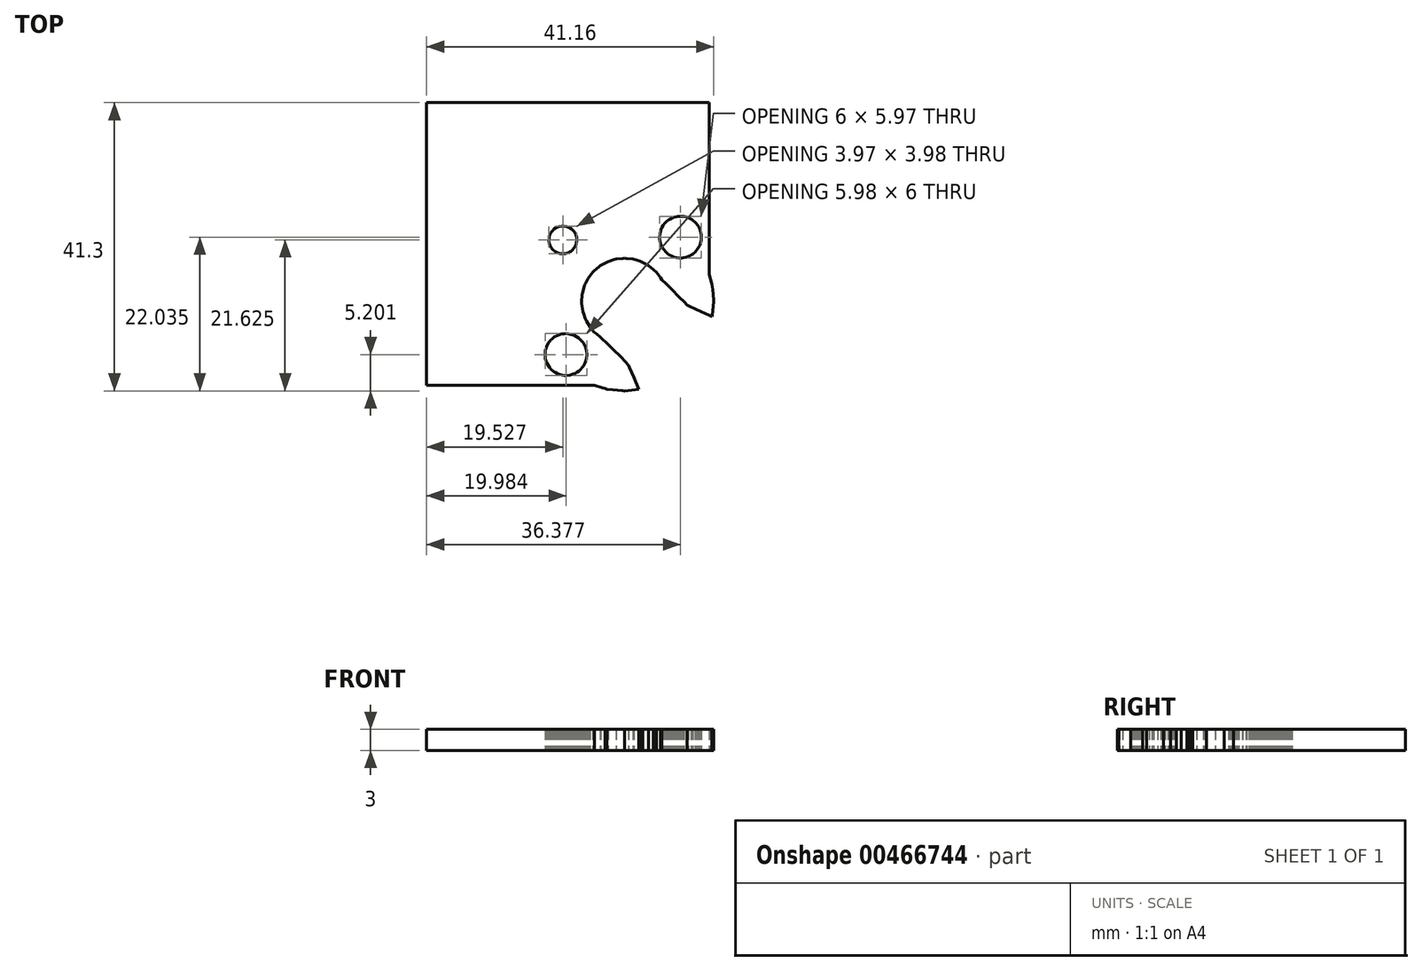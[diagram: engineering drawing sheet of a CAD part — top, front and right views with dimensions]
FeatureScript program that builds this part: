
annotation { "Feature Type Name" : "Feature", "Feature Type Description" : "" }
export const myFeature = defineFeature(function(context is Context, id is Id, definition is map)
    precondition{}
    {
        {
            var Q0;
            Q0=qCreatedBy(makeId("Top.planeOp"),FACE);
            var sketch = newSketch(context, id + "F0", { "sketchPlane" : qUnion([Q0])});
            skLineSegment(sketch, "E0", {"start": v(-20.58, -19.85) * mm, "end": v(-20.58, 20.65) * mm});
            skLineSegment(sketch, "E1", {"start": v(-20.58, 20.65) * mm, "end": v(19.92, 20.65) * mm});
            skLineSegment(sketch, "E2", {"start": v(19.92, 20.65) * mm, "end": v(19.92, -4) * mm});
            skLineSegment(sketch, "E3", {"start": v(19.92, -4) * mm, "end": v(20.25, -5.09) * mm});
            skLineSegment(sketch, "E4", {"start": v(20.25, -5.09) * mm, "end": v(20.33, -5.35) * mm});
            skLineSegment(sketch, "E5", {"start": v(20.33, -5.35) * mm, "end": v(20.4, -6.13) * mm});
            skLineSegment(sketch, "E6", {"start": v(20.4, -6.13) * mm, "end": v(20.55, -7.57) * mm});
            skLineSegment(sketch, "E7", {"start": v(20.55, -7.57) * mm, "end": v(20.58, -7.85) * mm});
            skLineSegment(sketch, "E8", {"start": v(20.58, -7.85) * mm, "end": v(20.38, -9.83) * mm});
            skLineSegment(sketch, "E9", {"start": v(20.38, -9.83) * mm, "end": v(20.3, -10.01) * mm});
            skLineSegment(sketch, "E10", {"start": v(20.3, -10.01) * mm, "end": v(19.9, -9.82) * mm});
            skLineSegment(sketch, "E11", {"start": v(19.9, -9.82) * mm, "end": v(18.76, -9.29) * mm});
            skLineSegment(sketch, "E12", {"start": v(18.76, -9.29) * mm, "end": v(17.15, -8.53) * mm});
            skLineSegment(sketch, "E13", {"start": v(17.15, -8.53) * mm, "end": v(16.75, -8.34) * mm});
            skLineSegment(sketch, "E14", {"start": v(16.75, -8.34) * mm, "end": v(16.35, -7.93) * mm});
            skLineSegment(sketch, "E15", {"start": v(16.35, -7.93) * mm, "end": v(15.6, -7.2) * mm});
            skLineSegment(sketch, "E16", {"start": v(15.6, -7.2) * mm, "end": v(14.5, -6.08) * mm});
            skLineSegment(sketch, "E17", {"start": v(14.5, -6.08) * mm, "end": v(14.13, -5.71) * mm});
            skLineSegment(sketch, "E18", {"start": v(14.13, -5.71) * mm, "end": v(13.74, -5.33) * mm});
            skLineSegment(sketch, "E19", {"start": v(13.74, -5.33) * mm, "end": v(13.12, -4.7) * mm});
            skLineSegment(sketch, "E20", {"start": v(13.12, -4.7) * mm, "end": v(12.95, -4.4) * mm});
            skLineSegment(sketch, "E21", {"start": v(12.95, -4.4) * mm, "end": v(12.37, -3.69) * mm});
            skLineSegment(sketch, "E22", {"start": v(12.37, -3.69) * mm, "end": v(11.95, -3.26) * mm});
            skLineSegment(sketch, "E23", {"start": v(11.95, -3.26) * mm, "end": v(11.25, -2.68) * mm});
            skLineSegment(sketch, "E24", {"start": v(11.25, -2.68) * mm, "end": v(10.4, -2.23) * mm});
            skLineSegment(sketch, "E25", {"start": v(10.4, -2.23) * mm, "end": v(10.03, -2.07) * mm});
            skLineSegment(sketch, "E26", {"start": v(10.03, -2.07) * mm, "end": v(9.6, -1.94) * mm});
            skLineSegment(sketch, "E27", {"start": v(9.6, -1.94) * mm, "end": v(9.01, -1.76) * mm});
            skLineSegment(sketch, "E28", {"start": v(9.01, -1.76) * mm, "end": v(8.06, -1.67) * mm});
            skLineSegment(sketch, "E29", {"start": v(8.06, -1.67) * mm, "end": v(7.8, -1.64) * mm});
            skLineSegment(sketch, "E30", {"start": v(7.8, -1.64) * mm, "end": v(7.55, -1.67) * mm});
            skLineSegment(sketch, "E31", {"start": v(7.55, -1.67) * mm, "end": v(6.6, -1.76) * mm});
            skLineSegment(sketch, "E32", {"start": v(6.6, -1.76) * mm, "end": v(6.35, -1.84) * mm});
            skLineSegment(sketch, "E33", {"start": v(6.35, -1.84) * mm, "end": v(5.44, -2.11) * mm});
            skLineSegment(sketch, "E34", {"start": v(5.44, -2.11) * mm, "end": v(5.2, -2.23) * mm});
            skLineSegment(sketch, "E35", {"start": v(5.2, -2.23) * mm, "end": v(4.32, -2.72) * mm});
            skLineSegment(sketch, "E36", {"start": v(4.32, -2.72) * mm, "end": v(4.17, -2.85) * mm});
            skLineSegment(sketch, "E37", {"start": v(4.17, -2.85) * mm, "end": v(3.77, -3.18) * mm});
            skLineSegment(sketch, "E38", {"start": v(3.77, -3.18) * mm, "end": v(3.43, -3.45) * mm});
            skLineSegment(sketch, "E39", {"start": v(3.43, -3.45) * mm, "end": v(3.24, -3.69) * mm});
            skLineSegment(sketch, "E40", {"start": v(3.24, -3.69) * mm, "end": v(2.63, -4.44) * mm});
            skLineSegment(sketch, "E41", {"start": v(2.63, -4.44) * mm, "end": v(2.54, -4.62) * mm});
            skLineSegment(sketch, "E42", {"start": v(2.54, -4.62) * mm, "end": v(2.2, -5.26) * mm});
            skLineSegment(sketch, "E43", {"start": v(2.2, -5.26) * mm, "end": v(2.09, -5.46) * mm});
            skLineSegment(sketch, "E44", {"start": v(2.09, -5.46) * mm, "end": v(2.01, -5.7) * mm});
            skLineSegment(sketch, "E45", {"start": v(2.01, -5.7) * mm, "end": v(1.74, -6.62) * mm});
            skLineSegment(sketch, "E46", {"start": v(1.74, -6.62) * mm, "end": v(1.71, -6.88) * mm});
            skLineSegment(sketch, "E47", {"start": v(1.71, -6.88) * mm, "end": v(1.62, -7.83) * mm});
            skLineSegment(sketch, "E48", {"start": v(1.62, -7.83) * mm, "end": v(1.64, -8.09) * mm});
            skLineSegment(sketch, "E49", {"start": v(1.64, -8.09) * mm, "end": v(1.81, -9.28) * mm});
            skLineSegment(sketch, "E50", {"start": v(1.81, -9.28) * mm, "end": v(1.92, -9.63) * mm});
            skLineSegment(sketch, "E51", {"start": v(1.92, -9.63) * mm, "end": v(2.11, -10.24) * mm});
            skLineSegment(sketch, "E52", {"start": v(2.11, -10.24) * mm, "end": v(2.34, -10.67) * mm});
            skLineSegment(sketch, "E53", {"start": v(2.34, -10.67) * mm, "end": v(2.83, -11.46) * mm});
            skLineSegment(sketch, "E54", {"start": v(2.83, -11.46) * mm, "end": v(3.17, -11.9) * mm});
            skLineSegment(sketch, "E55", {"start": v(3.17, -11.9) * mm, "end": v(3.43, -12.2) * mm});
            skLineSegment(sketch, "E56", {"start": v(3.43, -12.2) * mm, "end": v(3.77, -12.48) * mm});
            skLineSegment(sketch, "E57", {"start": v(3.77, -12.48) * mm, "end": v(4.37, -12.97) * mm});
            skLineSegment(sketch, "E58", {"start": v(4.37, -12.97) * mm, "end": v(5.44, -14) * mm});
            skLineSegment(sketch, "E59", {"start": v(5.44, -14) * mm, "end": v(6.14, -14.7) * mm});
            skLineSegment(sketch, "E60", {"start": v(6.14, -14.7) * mm, "end": v(7.25, -15.8) * mm});
            skLineSegment(sketch, "E61", {"start": v(7.25, -15.8) * mm, "end": v(7.85, -16.41) * mm});
            skLineSegment(sketch, "E62", {"start": v(7.85, -16.41) * mm, "end": v(8.34, -17) * mm});
            skLineSegment(sketch, "E63", {"start": v(8.34, -17) * mm, "end": v(8.5, -17.33) * mm});
            skLineSegment(sketch, "E64", {"start": v(8.5, -17.33) * mm, "end": v(9.15, -18.7) * mm});
            skLineSegment(sketch, "E65", {"start": v(9.15, -18.7) * mm, "end": v(9.83, -20.45) * mm});
            skLineSegment(sketch, "E66", {"start": v(9.83, -20.45) * mm, "end": v(7.78, -20.65) * mm});
            skLineSegment(sketch, "E67", {"start": v(7.78, -20.65) * mm, "end": v(7.5, -20.62) * mm});
            skLineSegment(sketch, "E68", {"start": v(7.5, -20.62) * mm, "end": v(6.06, -20.48) * mm});
            skLineSegment(sketch, "E69", {"start": v(6.06, -20.48) * mm, "end": v(5.28, -20.4) * mm});
            skLineSegment(sketch, "E70", {"start": v(5.28, -20.4) * mm, "end": v(5.02, -20.32) * mm});
            skLineSegment(sketch, "E71", {"start": v(5.02, -20.32) * mm, "end": v(4.68, -20.22) * mm});
            skLineSegment(sketch, "E72", {"start": v(4.68, -20.22) * mm, "end": v(3.45, -19.85) * mm});
            skLineSegment(sketch, "E73", {"start": v(3.45, -19.85) * mm, "end": v(-20.58, -19.85) * mm});
            skLineSegment(sketch, "E74", {"start": v(-3.59, -15.66) * mm, "end": v(-3.55, -14.86) * mm});
            skLineSegment(sketch, "E75", {"start": v(-3.55, -14.86) * mm, "end": v(-3.46, -14.58) * mm});
            skLineSegment(sketch, "E76", {"start": v(-3.46, -14.58) * mm, "end": v(-3.38, -14.3) * mm});
            skLineSegment(sketch, "E77", {"start": v(-3.38, -14.3) * mm, "end": v(-3.1, -13.78) * mm});
            skLineSegment(sketch, "E78", {"start": v(-3.1, -13.78) * mm, "end": v(-2.91, -13.55) * mm});
            skLineSegment(sketch, "E79", {"start": v(-2.91, -13.55) * mm, "end": v(-2.78, -13.4) * mm});
            skLineSegment(sketch, "E80", {"start": v(-2.78, -13.4) * mm, "end": v(-2.65, -13.26) * mm});
            skLineSegment(sketch, "E81", {"start": v(-2.65, -13.26) * mm, "end": v(-2.27, -12.95) * mm});
            skLineSegment(sketch, "E82", {"start": v(-2.27, -12.95) * mm, "end": v(-1.75, -12.68) * mm});
            skLineSegment(sketch, "E83", {"start": v(-1.75, -12.68) * mm, "end": v(-1.2, -12.5) * mm});
            skLineSegment(sketch, "E84", {"start": v(-1.2, -12.5) * mm, "end": v(-0.86, -12.47) * mm});
            skLineSegment(sketch, "E85", {"start": v(-0.86, -12.47) * mm, "end": v(-0.6, -12.45) * mm});
            skLineSegment(sketch, "E86", {"start": v(-0.6, -12.45) * mm, "end": v(-0.27, -12.48) * mm});
            skLineSegment(sketch, "E87", {"start": v(-0.27, -12.48) * mm, "end": v(-0.02, -12.52) * mm});
            skLineSegment(sketch, "E88", {"start": v(-0.02, -12.52) * mm, "end": v(0.24, -12.59) * mm});
            skLineSegment(sketch, "E89", {"start": v(0.24, -12.59) * mm, "end": v(0.54, -12.68) * mm});
            skLineSegment(sketch, "E90", {"start": v(0.54, -12.68) * mm, "end": v(0.84, -12.84) * mm});
            skLineSegment(sketch, "E91", {"start": v(0.84, -12.84) * mm, "end": v(1.18, -13.05) * mm});
            skLineSegment(sketch, "E92", {"start": v(1.18, -13.05) * mm, "end": v(1.59, -13.42) * mm});
            skLineSegment(sketch, "E93", {"start": v(1.59, -13.42) * mm, "end": v(1.89, -13.78) * mm});
            skLineSegment(sketch, "E94", {"start": v(1.89, -13.78) * mm, "end": v(2.08, -14.15) * mm});
            skLineSegment(sketch, "E95", {"start": v(2.08, -14.15) * mm, "end": v(2.2, -14.4) * mm});
            skLineSegment(sketch, "E96", {"start": v(2.2, -14.4) * mm, "end": v(2.34, -14.86) * mm});
            skLineSegment(sketch, "E97", {"start": v(2.34, -14.86) * mm, "end": v(2.4, -15.45) * mm});
            skLineSegment(sketch, "E98", {"start": v(2.4, -15.45) * mm, "end": v(2.34, -16.03) * mm});
            skLineSegment(sketch, "E99", {"start": v(2.34, -16.03) * mm, "end": v(2.16, -16.6) * mm});
            skLineSegment(sketch, "E100", {"start": v(2.16, -16.6) * mm, "end": v(2.03, -16.86) * mm});
            skLineSegment(sketch, "E101", {"start": v(2.03, -16.86) * mm, "end": v(1.89, -17.11) * mm});
            skLineSegment(sketch, "E102", {"start": v(1.89, -17.11) * mm, "end": v(1.72, -17.32) * mm});
            skLineSegment(sketch, "E103", {"start": v(1.72, -17.32) * mm, "end": v(1.5, -17.58) * mm});
            skLineSegment(sketch, "E104", {"start": v(1.5, -17.58) * mm, "end": v(1.22, -17.8) * mm});
            skLineSegment(sketch, "E105", {"start": v(1.22, -17.8) * mm, "end": v(0.96, -18) * mm});
            skLineSegment(sketch, "E106", {"start": v(0.96, -18) * mm, "end": v(0.72, -18.12) * mm});
            skLineSegment(sketch, "E107", {"start": v(0.72, -18.12) * mm, "end": v(0.51, -18.23) * mm});
            skLineSegment(sketch, "E108", {"start": v(0.51, -18.23) * mm, "end": v(-0.04, -18.4) * mm});
            skLineSegment(sketch, "E109", {"start": v(-0.04, -18.4) * mm, "end": v(-0.6, -18.45) * mm});
            skLineSegment(sketch, "E110", {"start": v(-0.6, -18.45) * mm, "end": v(-0.86, -18.42) * mm});
            skLineSegment(sketch, "E111", {"start": v(-0.86, -18.42) * mm, "end": v(-1.17, -18.4) * mm});
            skLineSegment(sketch, "E112", {"start": v(-1.17, -18.4) * mm, "end": v(-1.44, -18.32) * mm});
            skLineSegment(sketch, "E113", {"start": v(-1.44, -18.32) * mm, "end": v(-1.8, -18.2) * mm});
            skLineSegment(sketch, "E114", {"start": v(-1.8, -18.2) * mm, "end": v(-2.1, -18.04) * mm});
            skLineSegment(sketch, "E115", {"start": v(-2.1, -18.04) * mm, "end": v(-2.38, -17.85) * mm});
            skLineSegment(sketch, "E116", {"start": v(-2.38, -17.85) * mm, "end": v(-2.73, -17.57) * mm});
            skLineSegment(sketch, "E117", {"start": v(-2.73, -17.57) * mm, "end": v(-2.95, -17.3) * mm});
            skLineSegment(sketch, "E118", {"start": v(-2.95, -17.3) * mm, "end": v(-3.38, -16.6) * mm});
            skLineSegment(sketch, "E119", {"start": v(-3.38, -16.6) * mm, "end": v(-3.55, -16.03) * mm});
            skLineSegment(sketch, "E120", {"start": v(-3.55, -16.03) * mm, "end": v(-3.59, -15.66) * mm});
            skLineSegment(sketch, "E121", {"start": v(-3.04, 0.82) * mm, "end": v(-3.03, 1.21) * mm});
            skLineSegment(sketch, "E122", {"start": v(-3.03, 1.21) * mm, "end": v(-2.98, 1.48) * mm});
            skLineSegment(sketch, "E123", {"start": v(-2.98, 1.48) * mm, "end": v(-2.93, 1.68) * mm});
            skLineSegment(sketch, "E124", {"start": v(-2.93, 1.68) * mm, "end": v(-2.8, 1.95) * mm});
            skLineSegment(sketch, "E125", {"start": v(-2.8, 1.95) * mm, "end": v(-2.7, 2.12) * mm});
            skLineSegment(sketch, "E126", {"start": v(-2.7, 2.12) * mm, "end": v(-2.57, 2.27) * mm});
            skLineSegment(sketch, "E127", {"start": v(-2.57, 2.27) * mm, "end": v(-2.29, 2.54) * mm});
            skLineSegment(sketch, "E128", {"start": v(-2.29, 2.54) * mm, "end": v(-1.96, 2.76) * mm});
            skLineSegment(sketch, "E129", {"start": v(-1.96, 2.76) * mm, "end": v(-1.6, 2.9) * mm});
            skLineSegment(sketch, "E130", {"start": v(-1.6, 2.9) * mm, "end": v(-1.21, 2.97) * mm});
            skLineSegment(sketch, "E131", {"start": v(-1.21, 2.97) * mm, "end": v(-0.9, 2.97) * mm});
            skLineSegment(sketch, "E132", {"start": v(-0.9, 2.97) * mm, "end": v(-0.51, 2.9) * mm});
            skLineSegment(sketch, "E133", {"start": v(-0.51, 2.9) * mm, "end": v(-0.15, 2.76) * mm});
            skLineSegment(sketch, "E134", {"start": v(-0.15, 2.76) * mm, "end": v(0.18, 2.54) * mm});
            skLineSegment(sketch, "E135", {"start": v(0.18, 2.54) * mm, "end": v(0.6, 2.1) * mm});
            skLineSegment(sketch, "E136", {"start": v(0.6, 2.1) * mm, "end": v(0.8, 1.75) * mm});
            skLineSegment(sketch, "E137", {"start": v(0.8, 1.75) * mm, "end": v(0.9, 1.37) * mm});
            skLineSegment(sketch, "E138", {"start": v(0.9, 1.37) * mm, "end": v(0.93, 1.1) * mm});
            skLineSegment(sketch, "E139", {"start": v(0.93, 1.1) * mm, "end": v(0.93, 0.8) * mm});
            skLineSegment(sketch, "E140", {"start": v(0.93, 0.8) * mm, "end": v(0.9, 0.57) * mm});
            skLineSegment(sketch, "E141", {"start": v(0.9, 0.57) * mm, "end": v(0.84, 0.38) * mm});
            skLineSegment(sketch, "E142", {"start": v(0.84, 0.38) * mm, "end": v(0.72, 0.08) * mm});
            skLineSegment(sketch, "E143", {"start": v(0.72, 0.08) * mm, "end": v(0.5, -0.25) * mm});
            skLineSegment(sketch, "E144", {"start": v(0.5, -0.25) * mm, "end": v(0.39, -0.4) * mm});
            skLineSegment(sketch, "E145", {"start": v(0.39, -0.4) * mm, "end": v(0.23, -0.53) * mm});
            skLineSegment(sketch, "E146", {"start": v(0.23, -0.53) * mm, "end": v(0.08, -0.66) * mm});
            skLineSegment(sketch, "E147", {"start": v(0.08, -0.66) * mm, "end": v(-0.1, -0.77) * mm});
            skLineSegment(sketch, "E148", {"start": v(-0.1, -0.77) * mm, "end": v(-0.29, -0.86) * mm});
            skLineSegment(sketch, "E149", {"start": v(-0.29, -0.86) * mm, "end": v(-0.51, -0.93) * mm});
            skLineSegment(sketch, "E150", {"start": v(-0.51, -0.93) * mm, "end": v(-0.74, -0.99) * mm});
            skLineSegment(sketch, "E151", {"start": v(-0.74, -0.99) * mm, "end": v(-1.06, -1.02) * mm});
            skLineSegment(sketch, "E152", {"start": v(-1.06, -1.02) * mm, "end": v(-1.45, -0.98) * mm});
            skLineSegment(sketch, "E153", {"start": v(-1.45, -0.98) * mm, "end": v(-1.82, -0.87) * mm});
            skLineSegment(sketch, "E154", {"start": v(-1.82, -0.86) * mm, "end": v(-2.17, -0.68) * mm});
            skLineSegment(sketch, "E155", {"start": v(-2.17, -0.68) * mm, "end": v(-2.47, -0.43) * mm});
            skLineSegment(sketch, "E156", {"start": v(-2.47, -0.43) * mm, "end": v(-2.72, -0.13) * mm});
            skLineSegment(sketch, "E157", {"start": v(-2.72, -0.13) * mm, "end": v(-2.87, 0.15) * mm});
            skLineSegment(sketch, "E158", {"start": v(-2.87, 0.15) * mm, "end": v(-2.97, 0.44) * mm});
            skLineSegment(sketch, "E159", {"start": v(-2.97, 0.44) * mm, "end": v(-3.04, 0.82) * mm});
            skLineSegment(sketch, "E160", {"start": v(12.8, 1.38) * mm, "end": v(12.85, 1.87) * mm});
            skLineSegment(sketch, "E161", {"start": v(12.85, 1.87) * mm, "end": v(13, 2.47) * mm});
            skLineSegment(sketch, "E162", {"start": v(13, 2.47) * mm, "end": v(13.16, 2.78) * mm});
            skLineSegment(sketch, "E163", {"start": v(13.16, 2.78) * mm, "end": v(13.3, 3.05) * mm});
            skLineSegment(sketch, "E164", {"start": v(13.3, 3.05) * mm, "end": v(13.54, 3.33) * mm});
            skLineSegment(sketch, "E165", {"start": v(13.54, 3.33) * mm, "end": v(13.65, 3.47) * mm});
            skLineSegment(sketch, "E166", {"start": v(13.65, 3.47) * mm, "end": v(13.84, 3.63) * mm});
            skLineSegment(sketch, "E167", {"start": v(13.84, 3.63) * mm, "end": v(14.05, 3.81) * mm});
            skLineSegment(sketch, "E168", {"start": v(14.05, 3.81) * mm, "end": v(14.34, 3.99) * mm});
            skLineSegment(sketch, "E169", {"start": v(14.34, 3.99) * mm, "end": v(14.62, 4.14) * mm});
            skLineSegment(sketch, "E170", {"start": v(14.62, 4.14) * mm, "end": v(14.86, 4.22) * mm});
            skLineSegment(sketch, "E171", {"start": v(14.86, 4.22) * mm, "end": v(15.14, 4.3) * mm});
            skLineSegment(sketch, "E172", {"start": v(15.14, 4.3) * mm, "end": v(15.4, 4.34) * mm});
            skLineSegment(sketch, "E173", {"start": v(15.4, 4.34) * mm, "end": v(15.7, 4.37) * mm});
            skLineSegment(sketch, "E174", {"start": v(15.7, 4.37) * mm, "end": v(16.01, 4.36) * mm});
            skLineSegment(sketch, "E175", {"start": v(16.01, 4.36) * mm, "end": v(16.27, 4.33) * mm});
            skLineSegment(sketch, "E176", {"start": v(16.27, 4.33) * mm, "end": v(16.6, 4.25) * mm});
            skLineSegment(sketch, "E177", {"start": v(16.6, 4.25) * mm, "end": v(16.93, 4.16) * mm});
            skLineSegment(sketch, "E178", {"start": v(16.93, 4.16) * mm, "end": v(17.2, 4.01) * mm});
            skLineSegment(sketch, "E179", {"start": v(17.2, 4.01) * mm, "end": v(17.46, 3.88) * mm});
            skLineSegment(sketch, "E180", {"start": v(17.46, 3.88) * mm, "end": v(18.01, 3.39) * mm});
            skLineSegment(sketch, "E181", {"start": v(18.01, 3.39) * mm, "end": v(18.26, 3.08) * mm});
            skLineSegment(sketch, "E182", {"start": v(18.26, 3.08) * mm, "end": v(18.43, 2.8) * mm});
            skLineSegment(sketch, "E183", {"start": v(18.43, 2.8) * mm, "end": v(18.58, 2.5) * mm});
            skLineSegment(sketch, "E184", {"start": v(18.58, 2.5) * mm, "end": v(18.74, 1.96) * mm});
            skLineSegment(sketch, "E185", {"start": v(18.74, 1.96) * mm, "end": v(18.76, 1.71) * mm});
            skLineSegment(sketch, "E186", {"start": v(18.76, 1.71) * mm, "end": v(18.8, 1.37) * mm});
            skLineSegment(sketch, "E187", {"start": v(18.8, 1.37) * mm, "end": v(18.76, 1) * mm});
            skLineSegment(sketch, "E188", {"start": v(18.76, 1) * mm, "end": v(18.7, 0.67) * mm});
            skLineSegment(sketch, "E189", {"start": v(18.7, 0.67) * mm, "end": v(18.57, 0.23) * mm});
            skLineSegment(sketch, "E190", {"start": v(18.57, 0.23) * mm, "end": v(18.37, -0.15) * mm});
            skLineSegment(sketch, "E191", {"start": v(18.37, -0.15) * mm, "end": v(18.24, -0.35) * mm});
            skLineSegment(sketch, "E192", {"start": v(18.24, -0.35) * mm, "end": v(18.05, -0.58) * mm});
            skLineSegment(sketch, "E193", {"start": v(18.05, -0.58) * mm, "end": v(17.87, -0.78) * mm});
            skLineSegment(sketch, "E194", {"start": v(17.87, -0.78) * mm, "end": v(17.72, -0.9) * mm});
            skLineSegment(sketch, "E195", {"start": v(17.72, -0.9) * mm, "end": v(17.55, -1.05) * mm});
            skLineSegment(sketch, "E196", {"start": v(17.55, -1.05) * mm, "end": v(17.33, -1.19) * mm});
            skLineSegment(sketch, "E197", {"start": v(17.33, -1.19) * mm, "end": v(17.15, -1.29) * mm});
            skLineSegment(sketch, "E198", {"start": v(17.15, -1.29) * mm, "end": v(16.94, -1.4) * mm});
            skLineSegment(sketch, "E199", {"start": v(16.94, -1.4) * mm, "end": v(16.63, -1.49) * mm});
            skLineSegment(sketch, "E200", {"start": v(16.63, -1.49) * mm, "end": v(16.26, -1.57) * mm});
            skLineSegment(sketch, "E201", {"start": v(16.26, -1.57) * mm, "end": v(16, -1.6) * mm});
            skLineSegment(sketch, "E202", {"start": v(16, -1.6) * mm, "end": v(15.6, -1.6) * mm});
            skLineSegment(sketch, "E203", {"start": v(15.6, -1.6) * mm, "end": v(15.21, -1.56) * mm});
            skLineSegment(sketch, "E204", {"start": v(15.21, -1.56) * mm, "end": v(14.93, -1.48) * mm});
            skLineSegment(sketch, "E205", {"start": v(14.93, -1.48) * mm, "end": v(14.5, -1.31) * mm});
            skLineSegment(sketch, "E206", {"start": v(14.5, -1.31) * mm, "end": v(14.23, -1.17) * mm});
            skLineSegment(sketch, "E207", {"start": v(14.23, -1.17) * mm, "end": v(13.94, -0.96) * mm});
            skLineSegment(sketch, "E208", {"start": v(13.94, -0.96) * mm, "end": v(13.68, -0.74) * mm});
            skLineSegment(sketch, "E209", {"start": v(13.68, -0.74) * mm, "end": v(13.43, -0.44) * mm});
            skLineSegment(sketch, "E210", {"start": v(13.43, -0.44) * mm, "end": v(13.21, -0.11) * mm});
            skLineSegment(sketch, "E211", {"start": v(13.21, -0.12) * mm, "end": v(13.04, 0.21) * mm});
            skLineSegment(sketch, "E212", {"start": v(13.04, 0.21) * mm, "end": v(12.95, 0.47) * mm});
            skLineSegment(sketch, "E213", {"start": v(12.95, 0.47) * mm, "end": v(12.87, 0.76) * mm});
            skLineSegment(sketch, "E214", {"start": v(12.87, 0.76) * mm, "end": v(12.83, 1.1) * mm});
            skLineSegment(sketch, "E215", {"start": v(12.83, 1.1) * mm, "end": v(12.8, 1.38) * mm});
            skSolve(sketch);
        }
        {
            var Q0;
            Q0=makeQuery(id+"F0.imprint","IMPRINT",FACE,{"disambiguationData":[TD([[makeQuery(id+"F0.imprint","IMPRINT",EDGE,{"derivedFrom":sQuery(id+"F0.wireOp",EDGE,"E0")}),-1.0]])]});
            extrude(context, id + "F1", {"entities" : qUnion([Q0]), "depth" : 3 * mm});
        }
    });
